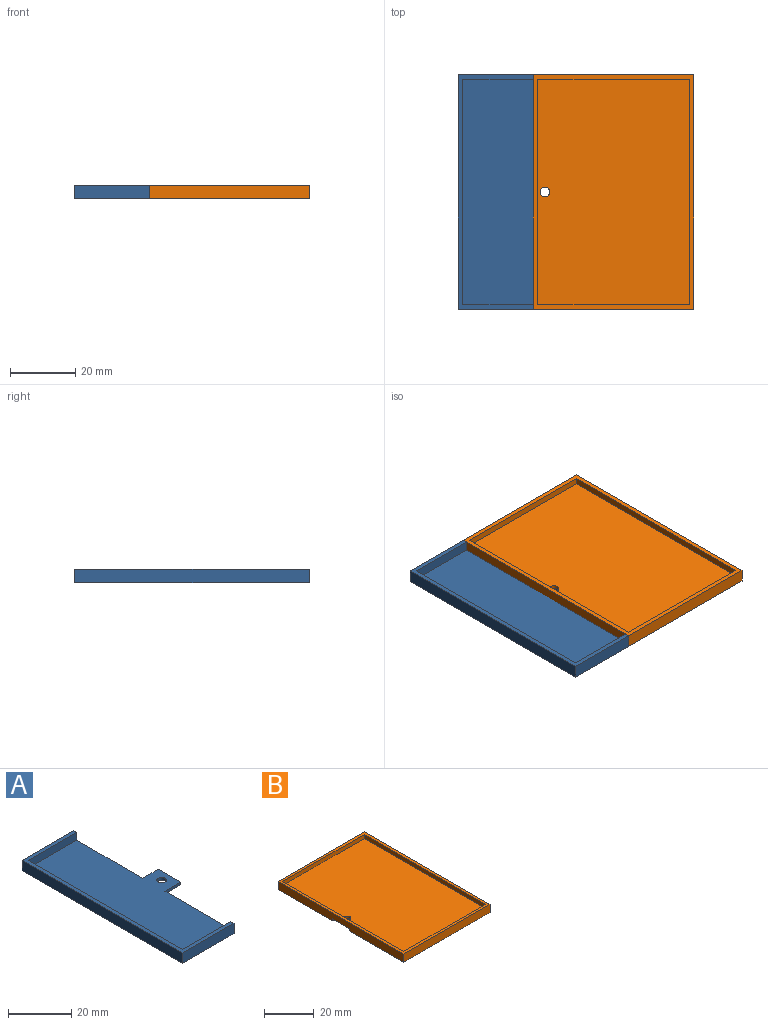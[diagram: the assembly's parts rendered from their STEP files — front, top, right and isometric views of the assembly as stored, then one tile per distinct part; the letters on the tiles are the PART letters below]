
ASSEMBLY  parts=2 mates=1
PART A: 15 faces, bbox 30x71.6x4 mm
  f0: plane 21.65x3mm, normal (0,1,0), area 64.9mm2, adj f1,f7,f8,f14
  f1: plane 68.9x3mm, normal (1,0,0), area 206.7mm2, adj f0,f2,f8,f14
  f2: plane 21.65x3mm, normal (0,-1,0), area 64.9mm2, adj f1,f3,f8,f14
  f3: plane 30.8x4mm, normal (1,0,0), area 34.8mm2, adj f2,f4,f8,f9,f12,f14
  f4: plane 23x4mm, normal (0,1,0), area 92mm2, adj f3,f5,f8,f9
  f5: plane 71.6x4mm, normal (-1,0,0), area 286.4mm2, adj f4,f6,f8,f9
  f6: plane 23x4mm, normal (0,-1,0), area 92mm2, adj f5,f7,f8,f9
  f7: plane 30.8x4mm, normal (1,0,0), area 34.8mm2, adj f0,f6,f8,f9,f10,f14
  f8: plane 71.6x23mm, normal (0,0,1), area 155.1mm2, adj f0,f1,f2,f3,f4,f5,f6,f7
  f9: plane 71.6x30mm, normal (0,0,-1), area 1709.7mm2, adj f3,f4,f5,f6,f7,f10,f11,f12
  f10: plane 7x1mm, normal (0,-1,0), area 7mm2, adj f7,f9,f11,f14
  f11: plane 10x1mm, normal (1,0,0), area 10mm2, adj f9,f10,f12,f14
  f12: plane 7x1mm, normal (0,1,0), area 7mm2, adj f3,f9,f11,f14
  f13: cylinder r=1.5mm len=3mm, axis (0,0,-1), area 9.4mm2, adj f9,f14
  f14: plane 68.9x28.65mm, normal (0,0,1), area 1554.6mm2, adj f0,f1,f2,f3,f7,f10,f11,f12
PART B: 16 faces, bbox 49x71.6x4 mm
  f0: plane 71.6x4mm, normal (-1,0,0), area 276.4mm2, adj f1,f5,f7,f9,f11,f12,f14
  f1: plane 71.6x49mm, normal (0,0,-1), area 3438.4mm2, adj f0,f5,f6,f7,f11,f12,f13
  f2: plane 46.3x2mm, normal (0,1,0), area 92.6mm2, adj f3,f8,f9,f10
  f3: plane 68.9x2mm, normal (1,0,0), area 137.8mm2, adj f2,f4,f9,f10
  f4: plane 46.3x2mm, normal (0,-1,0), area 92.6mm2, adj f3,f8,f9,f10
  f5: plane 49x4mm, normal (0,-1,0), area 196mm2, adj f0,f1,f6,f9
  f6: plane 71.6x4mm, normal (1,0,0), area 286.4mm2, adj f1,f5,f7,f9
  f7: plane 49x4mm, normal (0,1,0), area 196mm2, adj f0,f1,f6,f9
  f8: plane 68.9x2mm, normal (-1,0,0), area 137.8mm2, adj f2,f4,f9,f10
  f9: plane 71.6x49mm, normal (0,0,1), area 318.3mm2, adj f0,f2,f3,f4,f5,f6,f7,f8
  f10: plane 68.9x46.3mm, normal (0,0,1), area 3183mm2, adj f2,f3,f4,f8,f15
  f11: plane 7x1mm, normal (0,-1,0), area 7mm2, adj f0,f1,f13,f14
  f12: plane 7x1mm, normal (0,1,0), area 7mm2, adj f0,f1,f13,f14
  f13: plane 10x1mm, normal (-1,0,0), area 10mm2, adj f1,f11,f12,f14
  f14: plane 10x7mm, normal (0,0,-1), area 62.9mm2, adj f0,f11,f12,f13,f15
  f15: cylinder r=1.5mm len=3mm, axis (0,0,-1), area 9.4mm2, adj f10,f14
PLACE A t=(-38.79,4.94,7.83)mm
PLACE B t=(-2.79,4.94,7.83)mm
MATE fastened A.f13 <-> B.f15  axis (0,0,1) through (-23.79,4.94,8.83)mm
